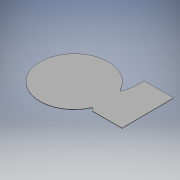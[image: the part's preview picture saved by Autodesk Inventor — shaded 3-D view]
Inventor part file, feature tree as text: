
AUTODESK INVENTOR PART (.ipt)
format: ipt  version: 2018 (Build 220112000, 112)  size: 116,224 bytes
history: native  units: mm
features: plane x1, extrude x1, sketch x1
ambient origin geometry x8: Origin, YZ Plane, XZ Plane, XY Plane, X Axis, Y Axis, Z Axis, Center Point
bodies: Volumenkörper1 (feature_tree)
feature tree (3):
  plane  "Arbeitsebene7"
  extrude  "Extrusion6"  Depth=1.0mm
  sketch  "Skizze6"  dims[d3=4.5mm d5=8.0mm d22=165.0mm d24=2.0mm d25=2.0mm d26=1.0mm d27=0.0mm]
